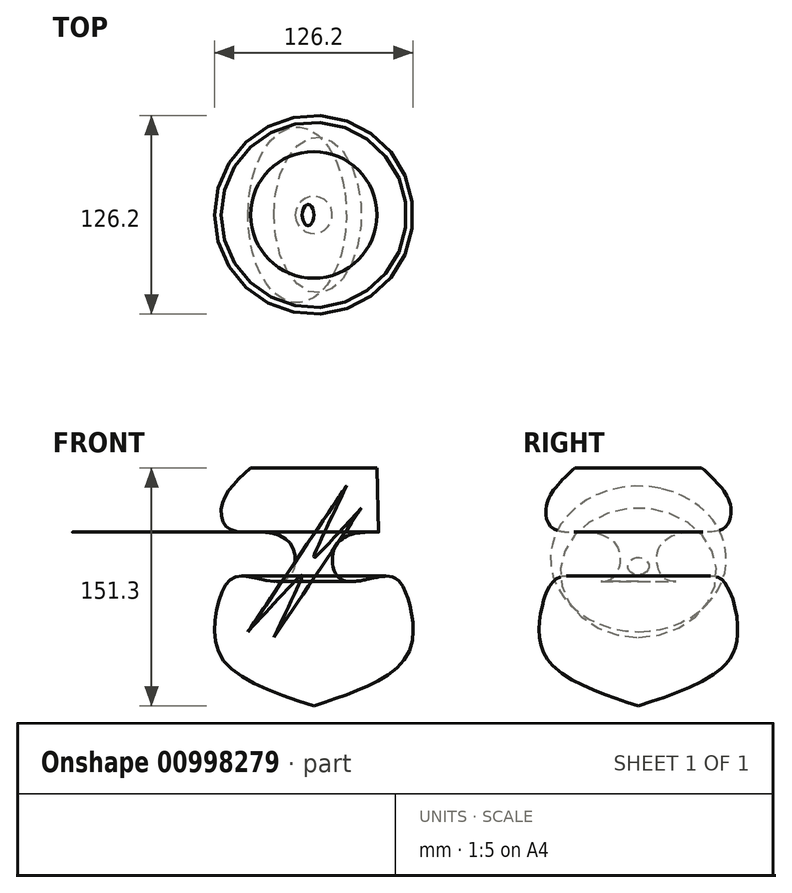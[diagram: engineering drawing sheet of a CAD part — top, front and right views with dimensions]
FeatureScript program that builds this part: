
annotation { "Feature Type Name" : "Feature", "Feature Type Description" : "" }
export const myFeature = defineFeature(function(context is Context, id is Id, definition is map)
    precondition{}
    {
        {
            var Q0;
            Q0=qCreatedBy(makeId("Front.planeOp"),FACE);
            var sketch = newSketch(context, id + "F0", { "sketchPlane" : qUnion([Q0])});
            skFitSpline(sketch, "E0", {"points": [v(-40.17, 70.28) * mm, v(-58.02, 47.96) * mm, v(-54.45, 31.9) * mm, v(-31.02, 29.22) * mm, v(-13.17, 19.4) * mm, v(-16.51, 0) * mm, v(-36.37, 0) * mm, v(-51.77, 0) * mm, v(-61.15, -17.65) * mm, v(-58.02, -51.12) * mm, v(0, -81.02) * mm], "startDerivative": vector(-215.6, -198.34) * mm, "endDerivative": vector(451.37, -148.96) * mm});
            skSolve(sketch);
        }
        {
            var Q0;
            Q0=qCreatedBy(makeId("Front.planeOp"),FACE);
            var sketch = newSketch(context, id + "F1", { "sketchPlane" : qUnion([Q0])});
            skLineSegment(sketch, "E1", {"start": v(0, 74.03) * mm, "end": v(0, -115.42) * mm});
            skSolve(sketch);
        }
        {
            var Q0;
            Q0=sQuery(id+"F0.wireOp",EDGE,"E0");
            var Q1;
            Q1=sQuery(id+"F1.wireOp",EDGE,"E1");
            revolve(context, id + "F2", {"bodyType" : ToolBodyType.SURFACE, "surfaceOperationType" : NewSurfaceOperationType.NEW, "surfaceEntities" : qUnion([Q0]), "axis" : qUnion([Q1]), "revolveType" : RevolveType.FULL});
        }
        {
            var Q0;
            Q0=qCreatedBy(makeId("Right.planeOp"),FACE);
            var sketch = newSketch(context, id + "F3", { "sketchPlane" : qUnion([Q0])});
            skLineSegment(sketch, "E2", {"start": v(-52.55, 28.02) * mm, "end": v(49.4, 0) * mm});
            skSolve(sketch);
        }
        {
            var Q0;
            Q0=qCreatedBy(makeId("Front.planeOp"),FACE);
            var sketch = newSketch(context, id + "F4", { "sketchPlane" : qUnion([Q0])});
            skLineSegment(sketch, "E3", {"start": v(-85.82, 63.27) * mm, "end": v(94.11, -58.4) * mm});
            skSolve(sketch);
        }
        {
            var Q0;
            Q0=sQuery(id+"F3.wireOp",EDGE,"E2");
            var Q1;
            Q1=sQuery(id+"F4.wireOp",EDGE,"E3");
            revolve(context, id + "F5", {"bodyType" : ToolBodyType.SURFACE, "surfaceOperationType" : NewSurfaceOperationType.NEW, "surfaceEntities" : qUnion([Q0]), "axis" : qUnion([Q1]), "revolveType" : RevolveType.FULL});
        }
    });
